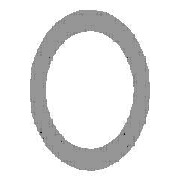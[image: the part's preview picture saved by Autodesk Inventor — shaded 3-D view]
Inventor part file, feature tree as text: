
AUTODESK INVENTOR PART (.ipt)
format: ipt  version: 2013 (Build 170138000, 138)  size: 114,176 bytes
history: native  units: mm (DEFAULTED — no unit token found)
features: other x4, plane x4, sketch x4, extrude x1
ambient origin geometry x8: Origin, YZ Plane, XZ Plane, XY Plane, X Axis, Y Axis, Z Axis, Center Point
bodies: Solid1 (feature_tree), Body (feature_tree)
feature tree (13):
  parser-record x1  (decoder bookkeeping rows leaked as tree rows — omitted from the tree; the rows remain in map.json)
  other  "Driven Length"
  other  "Start plane"
  other  "End plane"
  plane  "Work Plane4"
  plane  "Work Plane5"
  plane  "Work Plane6"
  extrude  "Extrusion2"  Depth=3.3782mm
  sketch  "Sketch"  dims[d5=508.0mm d6=90.0deg d7=508.0mm d8=3.302mm d9=0.0mm]
  sketch  "Sketch3"  dims[d0=33.401mm d1=3.3782mm]
  plane  "Work Plane3"
  sketch  "Sketch4"  dims[d2=508.0mm d3=0.0mm]
  sketch  "Sketch5"  dims[d4=-0.0mm]
